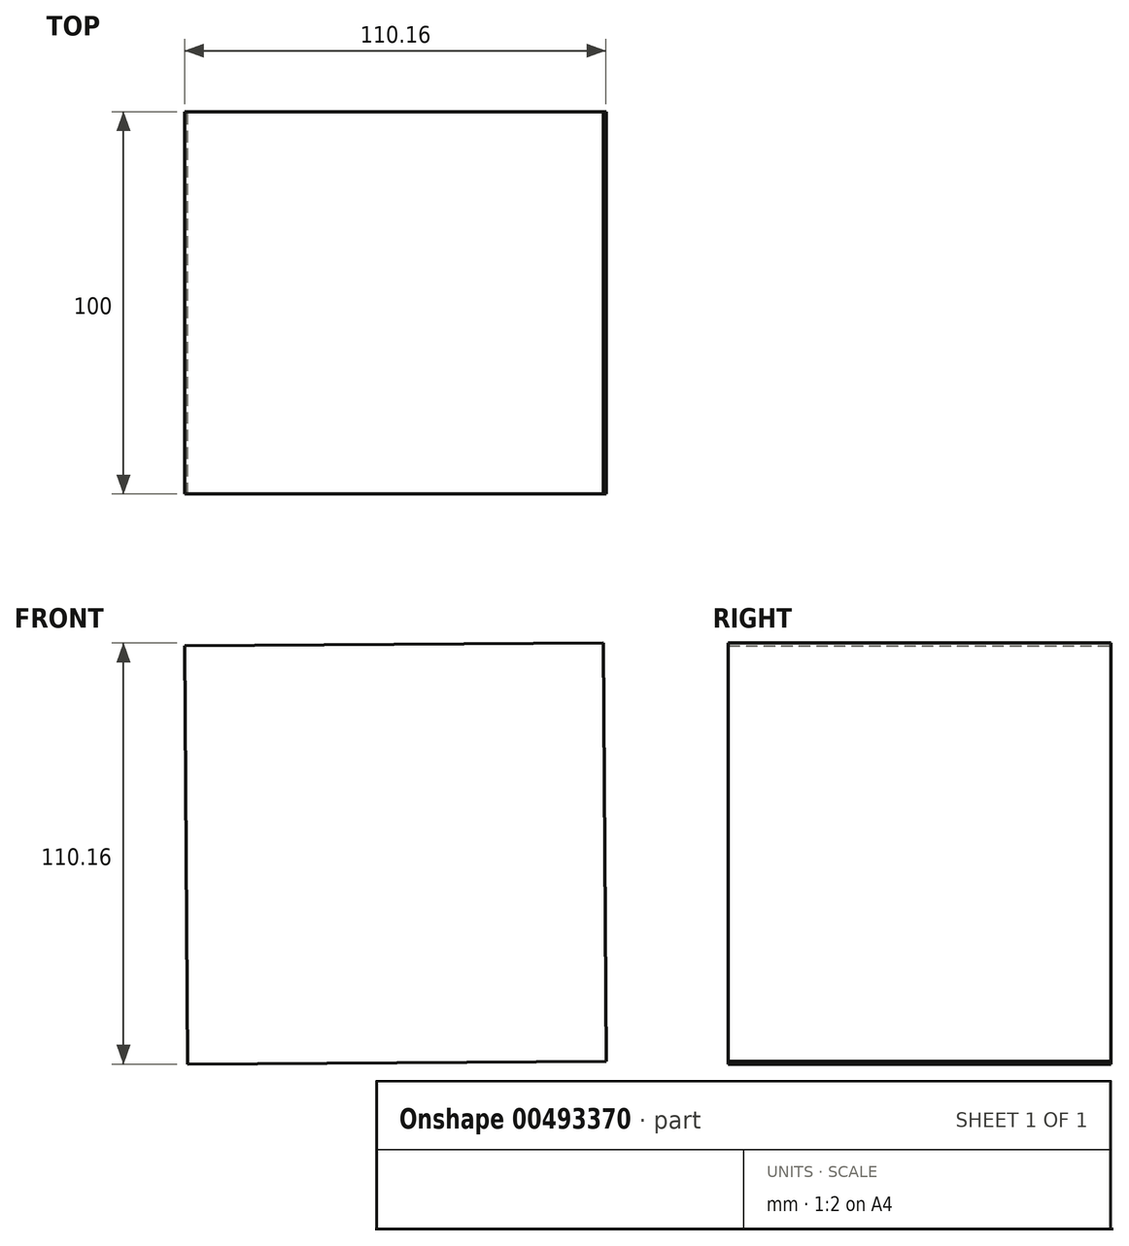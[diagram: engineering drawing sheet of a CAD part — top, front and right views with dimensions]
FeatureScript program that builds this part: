
annotation { "Feature Type Name" : "Feature", "Feature Type Description" : "" }
export const myFeature = defineFeature(function(context is Context, id is Id, definition is map)
    precondition{}
    {
        {
            var Q0;
            Q0=qCreatedBy(makeId("Front.planeOp"),FACE);
            var sketch = newSketch(context, id + "F0", { "sketchPlane" : qUnion([Q0])});
            skCircle(sketch, "E0.cCircle", {"center": v(0, 0) * mm, "radius": 77.4 * mm, "construction": true});
            skLineSegment(sketch, "E0.0", {"start": v(-55.08, 54.36) * mm, "end": v(54.36, 55.08) * mm});
            skLineSegment(sketch, "E0.1", {"start": v(54.36, 55.08) * mm, "end": v(55.08, -54.36) * mm});
            skLineSegment(sketch, "E0.2", {"start": v(55.08, -54.36) * mm, "end": v(-54.36, -55.08) * mm});
            skLineSegment(sketch, "E0.3", {"start": v(-54.36, -55.08) * mm, "end": v(-55.08, 54.36) * mm});
            skSolve(sketch);
        }
        {
            var Q0;
            Q0=makeQuery(id+"F0.imprint","IMPRINT",FACE,{"disambiguationData":[TD([[makeQuery(id+"F0.imprint","IMPRINT",EDGE,{"derivedFrom":sQuery(id+"F0.wireOp",EDGE,"E0.0")}),-1.0]])]});
            extrude(context, id + "F1", {"entities" : qUnion([Q0]), "endBound" : BoundingType.SYMMETRIC, "depth" : 100 * mm});
        }
    });
